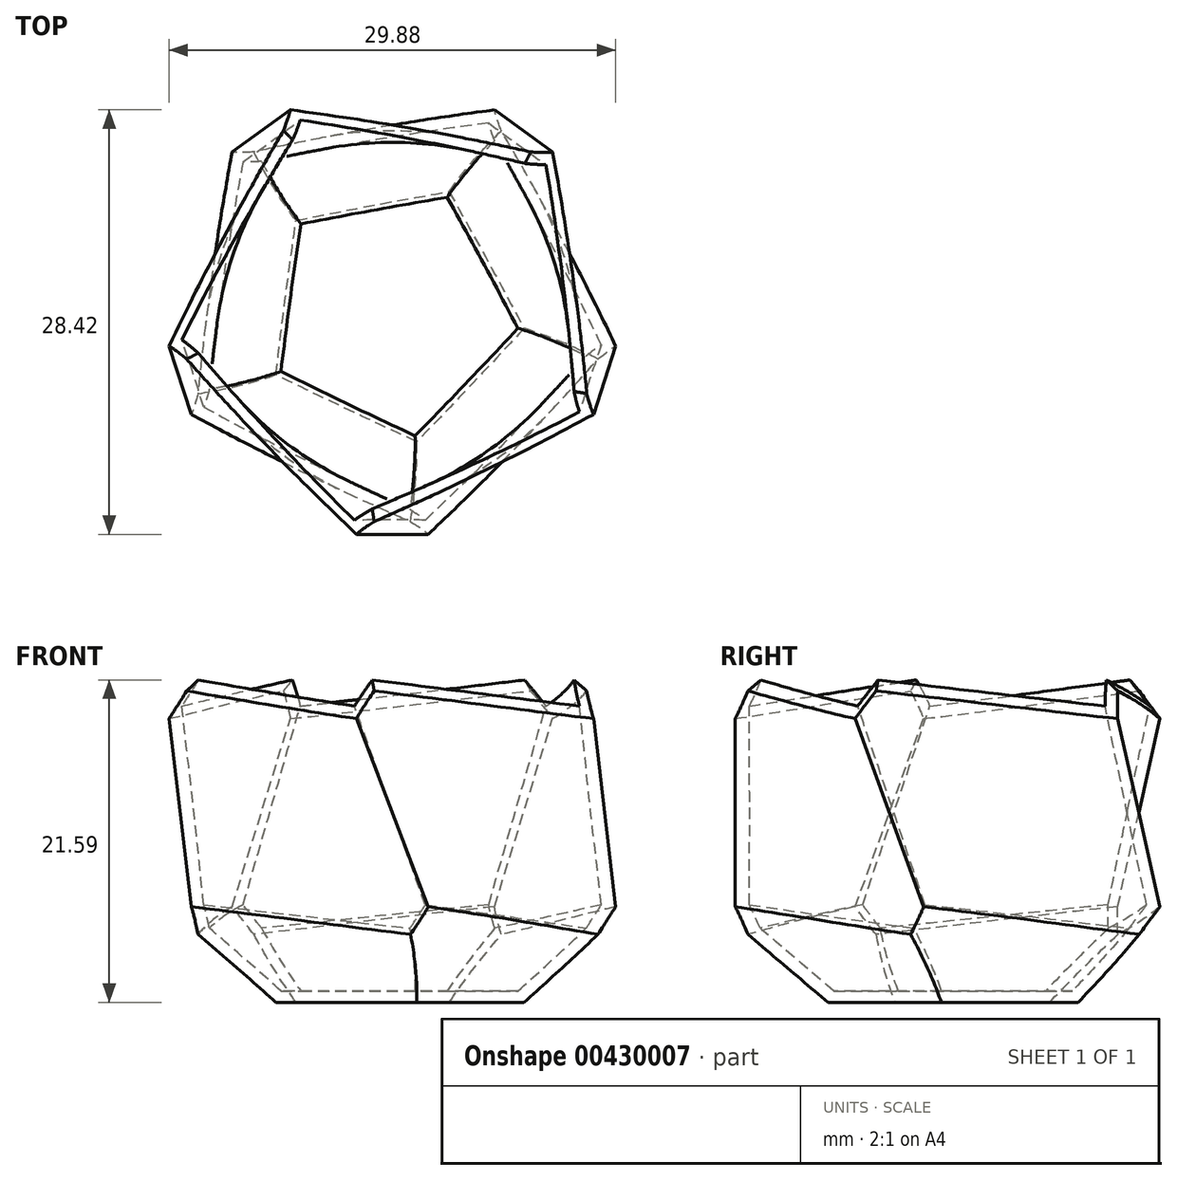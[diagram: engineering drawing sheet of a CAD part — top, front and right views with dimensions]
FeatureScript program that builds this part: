
annotation { "Feature Type Name" : "Feature", "Feature Type Description" : "" }
export const myFeature = defineFeature(function(context is Context, id is Id, definition is map)
    precondition{}
    {
        {
            var Q0;
            Q0=qCreatedBy(makeId("Top.planeOp"),FACE);
            var sketch = newSketch(context, id + "F0", { "sketchPlane" : qUnion([Q0])});
            skCircle(sketch, "E0.cCircle", {"center": v(0, 0) * mm, "radius": 12.7 * mm, "construction": true});
            skLineSegment(sketch, "E0.0", {"start": v(-12.7, -9.23) * mm, "end": v(-12.7, 9.23) * mm});
            skLineSegment(sketch, "E0.1", {"start": v(-12.7, 9.23) * mm, "end": v(4.85, 14.93) * mm});
            skLineSegment(sketch, "E0.2", {"start": v(4.85, 14.93) * mm, "end": v(15.7, 0) * mm});
            skLineSegment(sketch, "E0.3", {"start": v(15.7, 0) * mm, "end": v(4.85, -14.93) * mm});
            skLineSegment(sketch, "E0.4", {"start": v(4.85, -14.93) * mm, "end": v(-12.7, -9.23) * mm});
            skPoint(sketch, "E0.0.midPoint", {"position": v(-12.7, 0) * mm});
            skSolve(sketch);
        }
        {
            var Q0;
            Q0=makeQuery(id+"F0.imprint","IMPRINT",FACE,{"disambiguationData":[TD([[makeQuery(id+"F0.imprint","IMPRINT",EDGE,{"derivedFrom":sQuery(id+"F0.wireOp",EDGE,"E0.0")}),-1.0]])]});
            cPlane(context, id + "F1", {"entities" : qUnion([Q0]), "cplaneType" : CPlaneType.OFFSET, "offset" : 25.4 * mm, "width" : 152.4 * mm, "height" : 152.4 * mm});
        }
        {
            var Q0;
            Q0=qCreatedBy(id+"F1.planeOp",FACE);
            var sketch = newSketch(context, id + "F2", { "sketchPlane" : qUnion([Q0])});
            skCircle(sketch, "E1.cCircle", {"center": v(0, 0) * mm, "radius": 12.7 * mm, "construction": true});
            skLineSegment(sketch, "E1.0", {"start": v(12.7, 9.23) * mm, "end": v(12.7, -9.23) * mm});
            skLineSegment(sketch, "E1.1", {"start": v(12.7, -9.23) * mm, "end": v(-4.85, -14.93) * mm});
            skLineSegment(sketch, "E1.2", {"start": v(-4.85, -14.93) * mm, "end": v(-15.7, 0) * mm});
            skLineSegment(sketch, "E1.3", {"start": v(-15.7, 0) * mm, "end": v(-4.85, 14.93) * mm});
            skLineSegment(sketch, "E1.4", {"start": v(-4.85, 14.93) * mm, "end": v(12.7, 9.23) * mm});
            skPoint(sketch, "E1.0.midPoint", {"position": v(12.7, 0) * mm});
            skSolve(sketch);
        }
        {
            var Q0;
            Q0=makeQuery(id+"F0.imprint","IMPRINT",FACE,{"disambiguationData":[TD([[makeQuery(id+"F0.imprint","IMPRINT",EDGE,{"derivedFrom":sQuery(id+"F0.wireOp",EDGE,"E0.0")}),-1.0]])]});
            var Q1;
            Q1=makeQuery(id+"F2.imprint","IMPRINT",FACE,{"disambiguationData":[TD([[makeQuery(id+"F2.imprint","IMPRINT",EDGE,{"derivedFrom":sQuery(id+"F2.wireOp",EDGE,"E1.0")}),-1.0]])]});
            loft(context, id + "F3", {"sheetProfilesArray" : [{ "sheetProfileEntities" : qUnion([Q0]) }, { "sheetProfileEntities" : qUnion([Q1]) }]});
        }
        {
            var Q0;
            Q0=makeQuery(id+"F3.opLoft","CAP_FACE",FACE,{"disambiguationData":[OSD([makeQuery(id+"F0.imprint","IMPRINT",FACE,{"disambiguationData":[TD([[makeQuery(id+"F0.imprint","IMPRINT",EDGE,{"derivedFrom":sQuery(id+"F0.wireOp",EDGE,"E0.0")}),-1.0]])]})])],"isStart":true});
            chamfer(context, id + "F4", {"entities" : qUnion([Q0]), "width" : 5.08 * mm, "tangentPropagation" : true});
        }
        {
            var Q0;
            Q0=makeQuery(id+"F3.opLoft","CAP_FACE",FACE,{"disambiguationData":[OSD([makeQuery(id+"F2.imprint","IMPRINT",FACE,{"disambiguationData":[TD([[makeQuery(id+"F2.imprint","IMPRINT",EDGE,{"derivedFrom":sQuery(id+"F2.wireOp",EDGE,"E1.0")}),-1.0]])]})])],"isStart":true});
            shell(context, id + "F5", {"entities" : qUnion([Q0]), "thickness" : 0.76 * mm});
        }
        {
            var Q0;
            Q0=makeQuery(id+"F3.opLoft","MID_CAP_EDGE",EDGE,{"disambiguationData":[OSD([sQuery(id+"F2.wireOp",EDGE,"E1.0"),sQuery(id+"F2.wireOp",EDGE,"E1.3"),sQuery(id+"F2.wireOp",EDGE,"E1.4")])],"capPos":1.0});
            var Q1;
            Q1=makeQuery(id+"F3.opLoft","MID_CAP_EDGE",EDGE,{"disambiguationData":[OSD([sQuery(id+"F2.wireOp",EDGE,"E1.2"),sQuery(id+"F2.wireOp",EDGE,"E1.3"),sQuery(id+"F2.wireOp",EDGE,"E1.4")])],"capPos":1.0});
            var Q2;
            Q2=makeQuery(id+"F3.opLoft","MID_CAP_EDGE",EDGE,{"disambiguationData":[OSD([sQuery(id+"F2.wireOp",EDGE,"E1.1"),sQuery(id+"F2.wireOp",EDGE,"E1.2"),sQuery(id+"F2.wireOp",EDGE,"E1.3")])],"capPos":1.0});
            var Q3;
            Q3=makeQuery(id+"F3.opLoft","MID_CAP_EDGE",EDGE,{"disambiguationData":[OSD([sQuery(id+"F2.wireOp",EDGE,"E1.0"),sQuery(id+"F2.wireOp",EDGE,"E1.1"),sQuery(id+"F2.wireOp",EDGE,"E1.2")])],"capPos":1.0});
            var Q4;
            Q4=makeQuery(id+"F3.opLoft","MID_CAP_EDGE",EDGE,{"disambiguationData":[OSD([sQuery(id+"F2.wireOp",EDGE,"E1.0"),sQuery(id+"F2.wireOp",EDGE,"E1.1"),sQuery(id+"F2.wireOp",EDGE,"E1.4")])],"capPos":1.0});
            chamfer(context, id + "F6", {"entities" : qUnion([Q0, Q1, Q2, Q3, Q4]), "width" : 5.08 * mm, "tangentPropagation" : true});
        }
    });
